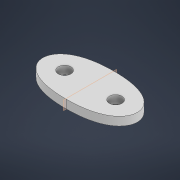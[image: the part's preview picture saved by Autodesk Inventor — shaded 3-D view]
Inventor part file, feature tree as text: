
AUTODESK INVENTOR PART (.ipt)
format: ipt  version: 2021 (Build 250183000, 183)  size: 108,032 bytes
history: native  units: mm
features: sketch x2, extrude x1, hole x1
ambient origin geometry x8: Origin, YZ Plane, XZ Plane, XY Plane, X Axis, Y Axis, Z Axis, Center Point
bodies: Solid1 (feature_tree)
feature tree (4):
  extrude  "Extrusion1"  Depth=12.113mm
  hole  "Hole1"  [1 undecoded]
  sketch  "Sketch1"  dims[d0=4.0mm d1=0.0mm d2=12.113mm]
  sketch  "Sketch2"  dims[d3=6.0mm d4=6.0mm d5=4.0mm d6=2.0mm d7=90.0deg d8=8.0mm d9=20.594885mm d10=12.113mm d11=0.0mm d12=0.0mm]
note: 1 required parameter value undecoded (feature->parameter linkage not recoverable at this tier; creation-order binding heuristic only, values carry confidence <= 0.55)
